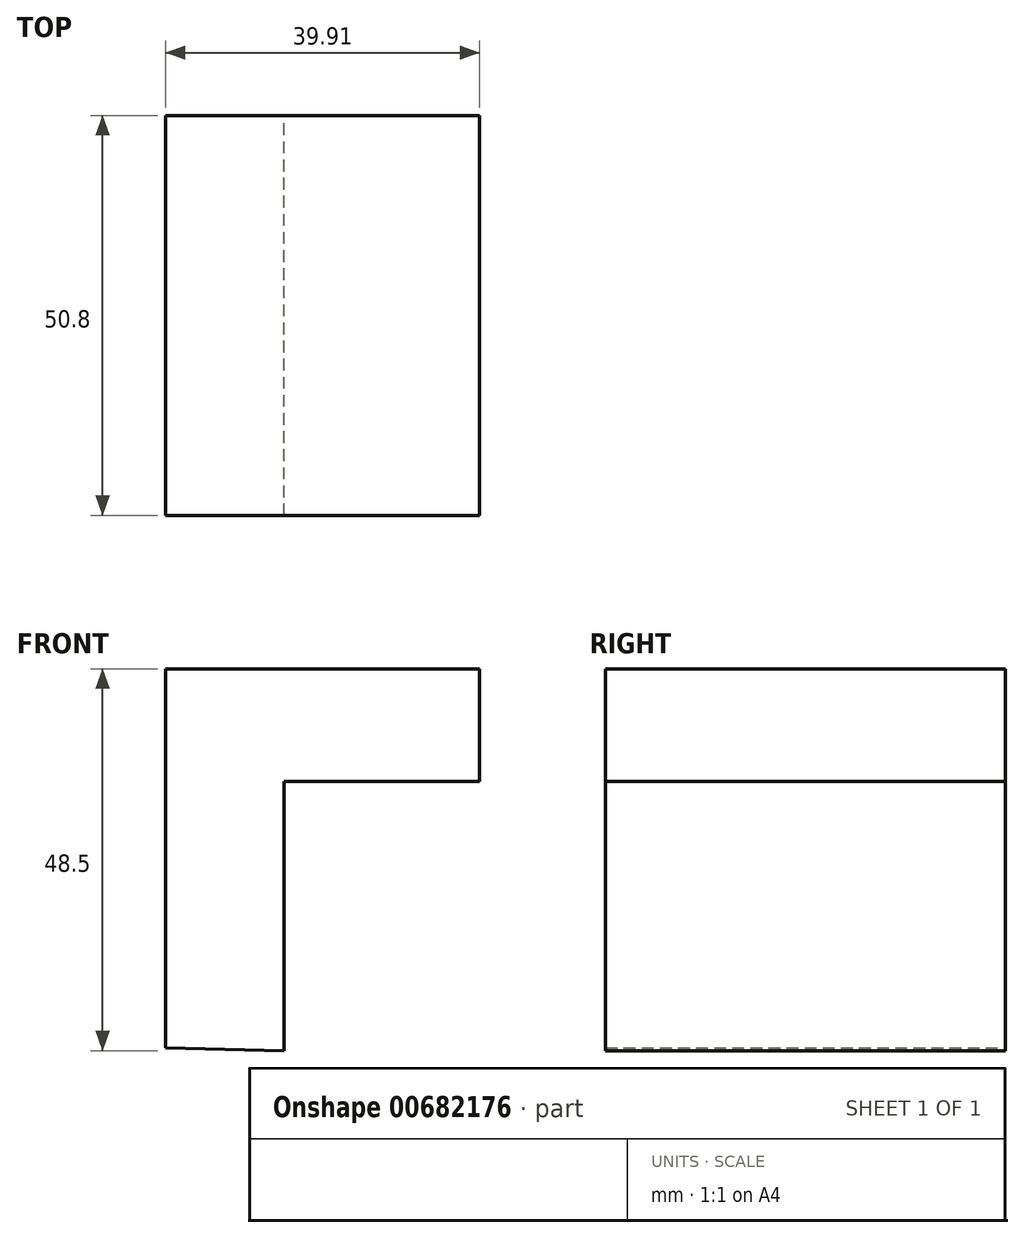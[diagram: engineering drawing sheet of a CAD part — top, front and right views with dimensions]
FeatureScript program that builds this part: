
annotation { "Feature Type Name" : "Feature", "Feature Type Description" : "" }
export const myFeature = defineFeature(function(context is Context, id is Id, definition is map)
    precondition{}
    {
        {
            var Q0;
            Q0=qCreatedBy(makeId("Front.planeOp"),FACE);
            var sketch = newSketch(context, id + "F0", { "sketchPlane" : qUnion([Q0])});
            skLineSegment(sketch, "E0", {"start": v(-71.9, 50.89) * mm, "end": v(-71.9, 2.77) * mm});
            skLineSegment(sketch, "E1", {"start": v(-71.9, 50.89) * mm, "end": v(-31.98, 50.89) * mm});
            skLineSegment(sketch, "E2", {"start": v(-31.98, 50.89) * mm, "end": v(-31.98, 36.57) * mm});
            skLineSegment(sketch, "E3", {"start": v(-31.98, 36.57) * mm, "end": v(-56.8, 36.57) * mm});
            skLineSegment(sketch, "E4", {"start": v(-56.8, 36.57) * mm, "end": v(-56.8, 2.39) * mm});
            skLineSegment(sketch, "E5", {"start": v(-56.8, 2.39) * mm, "end": v(-71.9, 2.77) * mm});
            skSolve(sketch);
        }
        {
            var Q0;
            Q0 = qSketchRegion(id + "F0", true);
            extrude(context, id + "F1", {"entities" : qUnion([Q0]), "depth" : 50.8 * mm, "offsetDistance" : 25.4 * mm});
        }
    });
